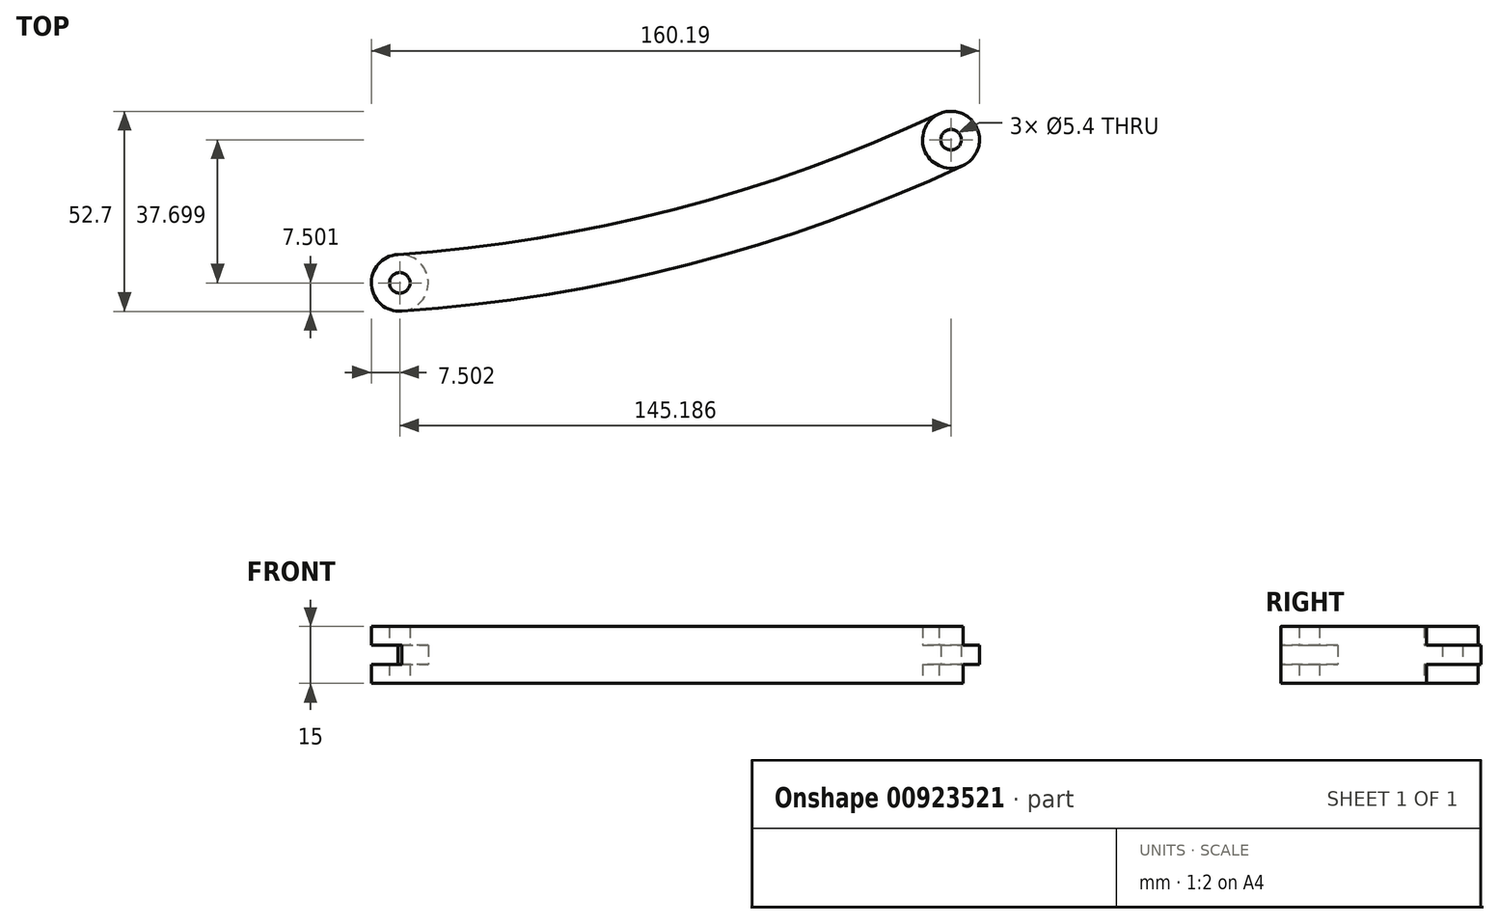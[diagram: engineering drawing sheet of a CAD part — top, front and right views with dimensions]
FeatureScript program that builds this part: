
annotation { "Feature Type Name" : "Feature", "Feature Type Description" : "" }
export const myFeature = defineFeature(function(context is Context, id is Id, definition is map)
    precondition{}
    {
        {
            var Q0;
            Q0=qCreatedBy(makeId("Top.planeOp"),FACE);
            var sketch = newSketch(context, id + "F0", { "sketchPlane" : qUnion([Q0])});
            skArc(sketch, "E0", {"start": v(-13.54, 4.71) * mm, "mid": v(59.43, 16.6) * mm, "end": v(128.97, 41.72) * mm});
            skArc(sketch, "E1.0", {"start": v(-12.51, -10.25) * mm, "mid": v(63.2, 2.08) * mm, "end": v(135.35, 28.14) * mm});
            skArc(sketch, "E2", {"start": v(135.35, 28.14) * mm, "mid": v(138.95, 38.12) * mm, "end": v(128.97, 41.72) * mm});
            skArc(sketch, "E3", {"start": v(-13.54, 4.71) * mm, "mid": v(-20.5, -3.29) * mm, "end": v(-12.51, -10.25) * mm});
            skCircle(sketch, "E4", {"center": v(132.16, 34.93) * mm, "radius": 2.7 * mm});
            skCircle(sketch, "E5", {"center": v(-13.03, -2.77) * mm, "radius": 2.7 * mm});
            skArc(sketch, "E6", {"start": v(-12.51, -10.25) * mm, "mid": v(-5.55, -2.25) * mm, "end": v(-13.54, 4.71) * mm});
            skArc(sketch, "E7", {"start": v(128.97, 41.72) * mm, "mid": v(125.37, 31.74) * mm, "end": v(135.35, 28.14) * mm});
            skSolve(sketch);
        }
        {
            var Q0;
            Q0=makeQuery(id+"F0.imprint","IMPRINT",FACE,{"disambiguationData":[TD([[makeQuery(id+"F0.imprint","IMPRINT",EDGE,{"derivedFrom":sQuery(id+"F0.wireOp",EDGE,"E0")}),-1.0]])]});
            extrude(context, id + "F1", {"entities" : qUnion([Q0]), "depth" : 15 * mm, "offsetDistance" : 25 * mm});
        }
        {
            var Q0;
            Q0=makeQuery(id+"F0.imprint","IMPRINT",FACE,{"disambiguationData":[TD([[makeQuery(id+"F0.imprint","IMPRINT",EDGE,{"derivedFrom":sQuery(id+"F0.wireOp",EDGE,"E3")}),1.0]])]});
            extrude(context, id + "F2", {"entities" : qUnion([Q0]), "operationType" : NewBodyOperationType.ADD, "depth" : 5 * mm, "offsetDistance" : 25 * mm, "hasSecondDirection" : true, "secondDirectionOppositeDirection" : false, "secondDirectionDepth" : 0 * mm});
        }
        {
            var Q0;
            Q0=makeQuery(id+"F0.imprint","IMPRINT",FACE,{"disambiguationData":[TD([[makeQuery(id+"F0.imprint","IMPRINT",EDGE,{"derivedFrom":sQuery(id+"F0.wireOp",EDGE,"E3")}),1.0]])]});
            extrude(context, id + "F3", {"entities" : qUnion([Q0]), "operationType" : NewBodyOperationType.ADD, "depth" : 15 * mm, "offsetDistance" : 25 * mm, "hasSecondDirection" : true, "secondDirectionOppositeDirection" : false, "secondDirectionDepth" : 10 * mm});
        }
        {
            var Q0;
            Q0=makeQuery(id+"F0.imprint","IMPRINT",FACE,{"disambiguationData":[TD([[makeQuery(id+"F0.imprint","IMPRINT",EDGE,{"derivedFrom":sQuery(id+"F0.wireOp",EDGE,"E2")}),1.0]])]});
            extrude(context, id + "F4", {"entities" : qUnion([Q0]), "operationType" : NewBodyOperationType.ADD, "depth" : 10 * mm, "offsetDistance" : 25 * mm, "hasSecondDirection" : true, "secondDirectionOppositeDirection" : false, "secondDirectionDepth" : 5 * mm});
        }
    });
